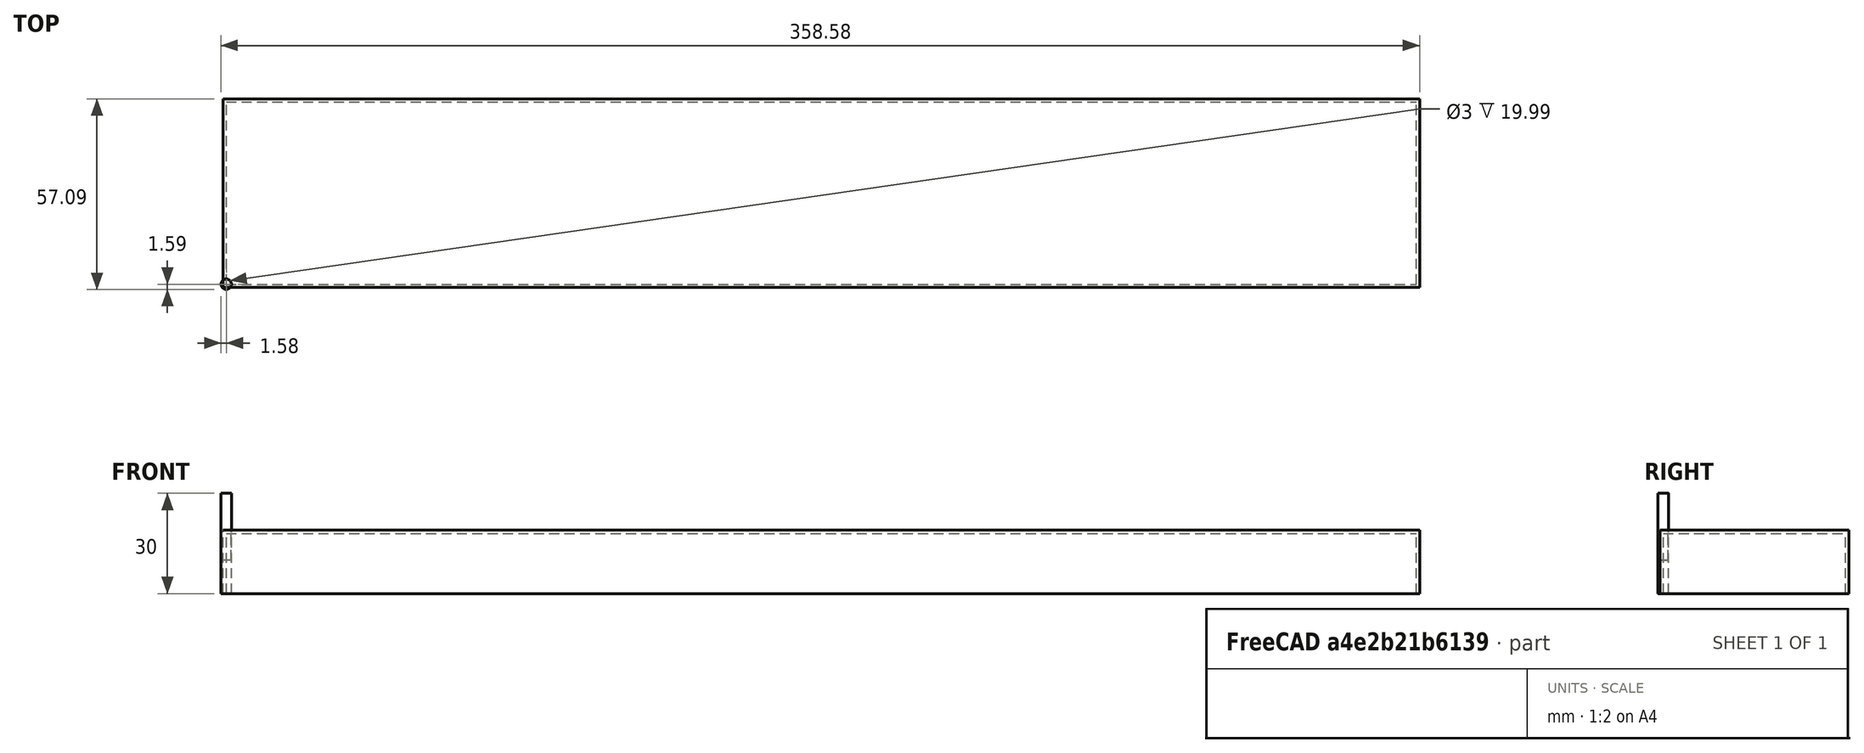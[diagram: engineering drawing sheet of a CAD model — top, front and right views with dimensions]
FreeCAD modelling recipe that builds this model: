
FCSTD DOCUMENT  (FreeCAD 0.21R31641 (Git))
Label: 456
License: All rights reserved
LicenseURL: http://en.wikipedia.org/wiki/All_rights_reserved
objects: Part::FeaturePython×3, App::DocumentObjectGroup×3, Path::FeaturePython×3, PartDesign::AdditiveBox×1, PartDesign::Body×1, App::FeaturePython×1
note: 7 computed .brp shape members not serialized (recipe doc carries the construction recipe); baked Part::Feature solids carry a one-line shape summary decoded from their .brp

FEATURE [PartDesign::AdditiveBox] Box
  AttacherType = Attacher::AttachEngine3D
  Height = 18
  Length = 356
  Width = 54.5
FEATURE [PartDesign::Body] Body
  Group = -> [Box]
  Origin = -> Origin
  Tip = -> Box
FEATURE [App::FeaturePython] SetupSheet  # Path/CAM operation (typed FeaturePython)
  ClearanceHeightExpression = OpStockZMax+SetupSheet.ClearanceHeightOffset
  ClearanceHeightOffset = 5
  CoolantMode = 0
  CoolantModes = None | Flood | Mist
  FinalDepthExpression = OpFinalDepth
  HorizRapid = 0
  ProfileDirection = 1
  ProfileprocessCircles = true
  ProfileprocessHoles = true
  ProfileprocessPerimeter = true
  SafeHeightExpression = OpStockZMax+SetupSheet.SafeHeightOffset
  SafeHeightOffset = 3
  StartDepthExpression = OpStartDepth
  StepDownExpression = OpToolDiameter
  VertRapid = 0
FEATURE [Part::FeaturePython] Clone  label="Model-Body"  # Draft clone (typed FeaturePython)
  AttacherType = Attacher::AttachEngine3D
  Fuse = false
  Objects = -> [Body]
  PathResource = Model
  Scale = (1,1,1)
FEATURE [App::DocumentObjectGroup] Model
  Group = -> [Clone]
FEATURE [Part::FeaturePython] ToolBit  label="3.175mm Endmill"  # Path/CAM toolbit (typed FeaturePython)
  BitPropertyNames = Chipload | CuttingEdgeHeight | Diameter | Flutes | Length | Material | ShankDiameter | SpindleDirection
  BitShape = <path>
  Chipload = 0
  CuttingEdgeHeight = 30
  Diameter = 3.17
  Flutes = 0
  Length = 10
  Material = 0
  ShankDiameter = 3
  ShapeName = endmill
  SpindleDirection = 0
FEATURE [Path::FeaturePython] __175mm_Endmill  label="3.175mm Endmill001"  # Path/CAM operation (typed FeaturePython)
  HorizFeed = 51.6667
  HorizRapid = 0
  SpindleDir = 0
  SpindleSpeed = 18000
  Tool = -> ToolBit
  ToolNumber = 1
  VertFeed = 16.6667
  VertRapid = 0
  expr: HorizRapid = SetupSheet.HorizRapid
  expr: VertRapid = SetupSheet.VertRapid
FEATURE [App::DocumentObjectGroup] Tools
  Group = -> [__175mm_Endmill]
FEATURE [Part::FeaturePython] Stock  # WARN: FeaturePython — macro-defined, semantics opaque (R4)
  Base = -> Model
  ExtXneg = 1
  ExtXpos = 1
  ExtYneg = 1
  ExtYpos = 1
  ExtZneg = 0
  ExtZpos = 1
  StockType = FromBase
FEATURE [Path::FeaturePython] Profile  # Path/CAM operation (typed FeaturePython)
  Active = true
  AreaParams:
    Tolerance = 1e-07
    FitArcs = True
    Simplify = False
    CleanDistance = 0.0
    Accuracy = 0.01
    Unit = 1.0
    MinArcPoints = 4
    MaxArcPoints = 100
    ClipperScale = 10000000.0
    Fill = 0
    Coplanar = 0
    Reorient = True
    Outline = False
    Explode = False
    OpenMode = 0
    Deflection = 0.01
    SubjectFill = 0
    ClipFill = 0
    Offset = 1.585
    ExtraPass = 0
    Stepover = 0.0
    LastStepover = 0.0
    JoinType = 0
    EndType = 0
    MiterLimit = 2.0
    RoundPrecision = 0.0
    PocketMode = 0
    ToolRadius = 1.0
    PocketExtraOffset = 0.0
    PocketStepover = 0.0
    PocketLastStepover = 0.0
    FromCenter = False
    Angle = 45.0
    AngleShift = 0.0
    Shift = 0.0
    Thicken = False
    SectionCount = -1
    Stepdown = 1.0
    SectionOffset = 0.0
    SectionTolerance = 1e-07
    SectionMode = 2
    Project = False
  ClearanceHeight = 24
  CoolantMode = 0
  CycleTime = 00:01:47
  Direction = 1
  FinalDepth = 0
  HandleMultipleFeatures = 0
  JoinType = 0
  MiterLimit = 0.1
  OffsetExtra = 0
  OpFinalDepth = 0
  OpStartDepth = 19
  OpStockZMax = 19
  OpStockZMin = 0
  OpToolDiameter = 3.17
  PathParams = {'orientation': 0, 'feedrate': 51.666666666666664, 'feedrate_v': 16.666666666666668, 'verbose': True, 'resume_height': 22.0, 'retraction': 24.0, 'return_end': True, 'preamble': False}
  SafeHeight = 22
  Side = 0
  SplitArcs = false
  StartDepth = 19
  StartPoint = (0,0,0)
  StepDown = 3.17
  ToolController = -> __175mm_Endmill
  UseComp = true
  UseStartPoint = false
  processCircles = true
  processHoles = true
  processPerimeter = true
  expr: ClearanceHeight = OpStockZMax + SetupSheet.ClearanceHeightOffset
  expr: FinalDepth = OpFinalDepth
  expr: SafeHeight = OpStockZMax + SetupSheet.SafeHeightOffset
  expr: StartDepth = OpStartDepth
  expr: StepDown = OpToolDiameter
FEATURE [App::DocumentObjectGroup] Operations
  Group = -> [Profile]
FEATURE [Path::FeaturePython] Job  # Path/CAM operation (typed FeaturePython)
  CycleTime = 00:01:47
  Fixtures = G54
  GeometryTolerance = 0.01
  JobType = 0
  LastPostProcessDate = 2023-01-28 19:14:19.707018
  LastPostProcessOutput = <userpath>/2411-26D9/Unnamed1.Job.tap
  Model = -> Model
  Operations = -> Operations
  OrderOutputBy = 0
  PostProcessor = 1
  PostProcessorOutputFile = %d.%j.tap
  SetupSheet = -> SetupSheet
  SplitOutput = false
  Stock = -> Stock
  Tools = -> Tools
note: 1 file-system path scrubbed to <path> (originals preserved in the JSON sidecar)
